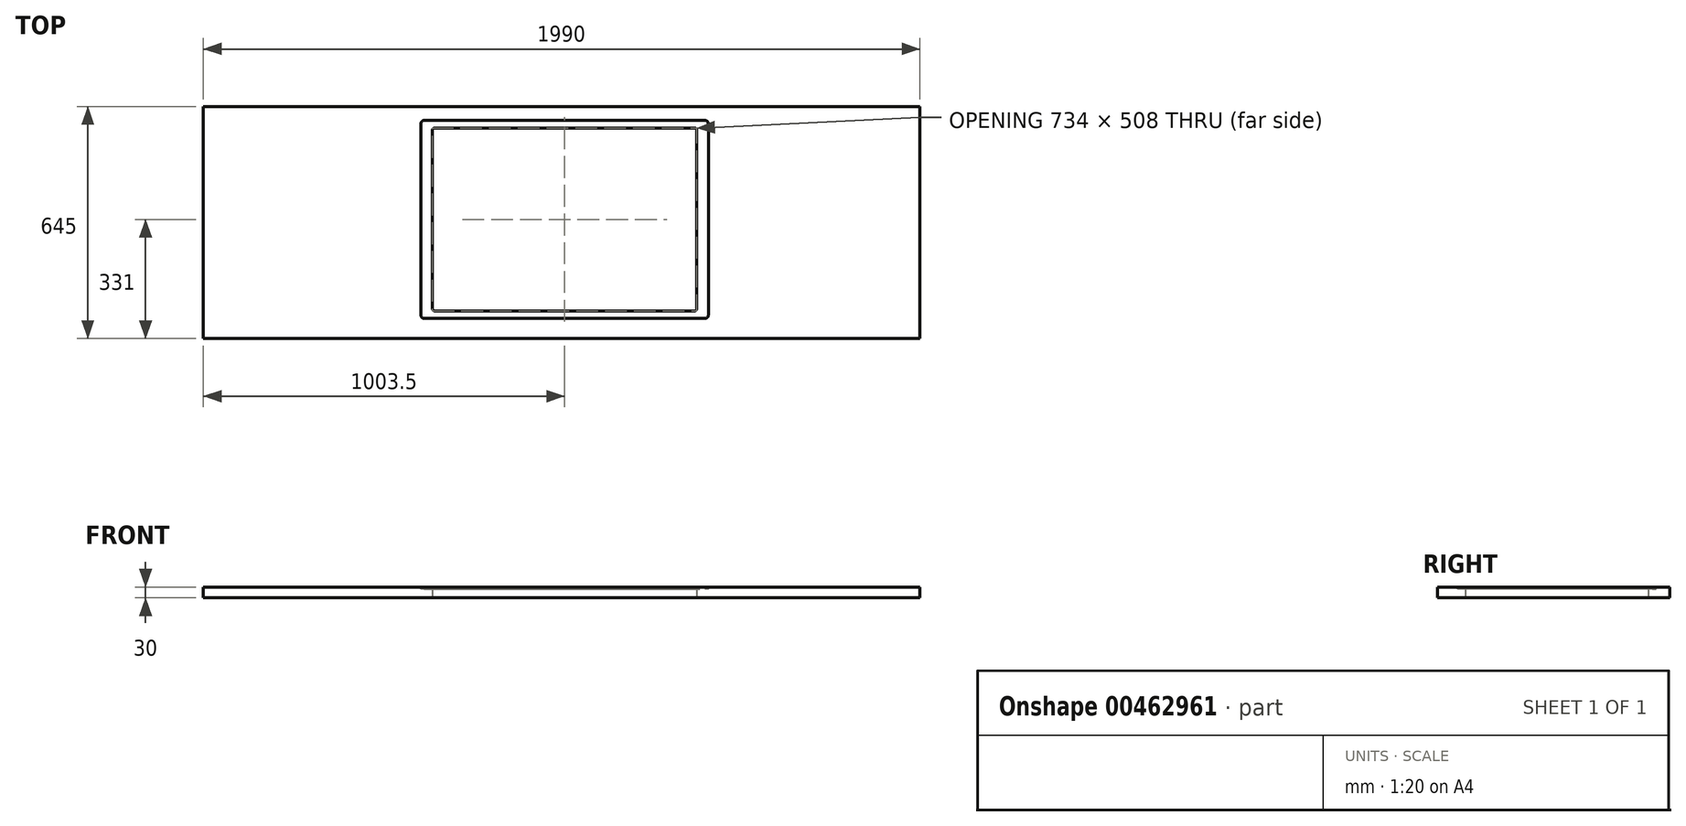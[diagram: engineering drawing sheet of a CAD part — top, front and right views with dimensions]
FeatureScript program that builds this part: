
annotation { "Feature Type Name" : "Feature", "Feature Type Description" : "" }
export const myFeature = defineFeature(function(context is Context, id is Id, definition is map)
    precondition{}
    {
        {
            var Q0;
            Q0=qCreatedBy(makeId("Top.planeOp"),FACE);
            var sketch = newSketch(context, id + "F0", { "sketchPlane" : qUnion([Q0])});
            skLineSegment(sketch, "E0.bottom", {"start": v(0, 0) * mm, "end": v(-1990, 0) * mm});
            skLineSegment(sketch, "E0.top", {"start": v(0, 645) * mm, "end": v(-1990, 645) * mm});
            skLineSegment(sketch, "E0.left", {"start": v(0, 0) * mm, "end": v(0, 645) * mm});
            skLineSegment(sketch, "E0.right", {"start": v(-1990, 0) * mm, "end": v(-1990, 645) * mm});
            skLineSegment(sketch, "E1.bottom", {"start": v(-1347.5, 585) * mm, "end": v(-625.5, 585) * mm});
            skLineSegment(sketch, "E1.top", {"start": v(-1347.5, 77) * mm, "end": v(-625.5, 77) * mm});
            skLineSegment(sketch, "E1.left", {"start": v(-1353.5, 579) * mm, "end": v(-1353.5, 83) * mm});
            skLineSegment(sketch, "E1.right", {"start": v(-619.5, 579) * mm, "end": v(-619.5, 83) * mm});
            skPoint(sketch, "E2.visualSharp", {"position": v(-1353.5, 585) * mm});
            skArc(sketch, "E2.filletArc", {"start": v(-1347.5, 585) * mm, "mid": v(-1351.74, 583.24) * mm, "end": v(-1353.5, 579) * mm});
            skPoint(sketch, "E3.visualSharp", {"position": v(-1353.5, 77) * mm});
            skArc(sketch, "E3.filletArc", {"start": v(-1353.5, 83) * mm, "mid": v(-1351.74, 78.76) * mm, "end": v(-1347.5, 77) * mm});
            skPoint(sketch, "E4.visualSharp", {"position": v(-619.5, 77) * mm});
            skArc(sketch, "E4.filletArc", {"start": v(-625.5, 77) * mm, "mid": v(-621.26, 78.76) * mm, "end": v(-619.5, 83) * mm});
            skPoint(sketch, "E5.visualSharp", {"position": v(-619.5, 585) * mm});
            skArc(sketch, "E5.filletArc", {"start": v(-619.5, 579) * mm, "mid": v(-621.26, 583.24) * mm, "end": v(-625.5, 585) * mm});
            skLineSegment(sketch, "E6", {"start": v(0, 322.5) * mm, "end": v(-1990, 322.5) * mm, "construction": true});
            skSolve(sketch);
        }
        {
            var Q0;
            Q0 = qSketchRegion(id + "F0", true);
            var Q1;
            Q1=makeQuery(id+"F0.imprint","IMPRINT",FACE,{"disambiguationData":[TD([[makeQuery(id+"F0.imprint","IMPRINT",EDGE,{"derivedFrom":sQuery(id+"F0.wireOp",EDGE,"E0.bottom")}),-1.0]])]});
            extrude(context, id + "F1", {"entities" : qUnion([Q0, Q1]), "depth" : 30 * mm});
        }
        {
            var Q0;
            Q0=makeQuery(id+"F1.opExtrude","CAP_FACE",FACE,{"disambiguationData":[OSD([sQuery(id+"F0.wireOp",EDGE,"E0.bottom"),sQuery(id+"F0.wireOp",EDGE,"E0.top"),sQuery(id+"F0.wireOp",EDGE,"E0.left"),sQuery(id+"F0.wireOp",EDGE,"E0.right"),sQuery(id+"F0.wireOp",EDGE,"E1.bottom"),sQuery(id+"F0.wireOp",EDGE,"E1.top"),sQuery(id+"F0.wireOp",EDGE,"E1.left"),sQuery(id+"F0.wireOp",EDGE,"E1.right"),sQuery(id+"F0.wireOp",EDGE,"E2.filletArc"),sQuery(id+"F0.wireOp",EDGE,"E3.filletArc"),sQuery(id+"F0.wireOp",EDGE,"E4.filletArc"),sQuery(id+"F0.wireOp",EDGE,"E5.filletArc")])],"isStart":false});
            var sketch = newSketch(context, id + "F2", { "sketchPlane" : qUnion([Q0])});
            skArc(sketch, "E7.0", {"start": v(-587.5, 597) * mm, "mid": v(-590.14, 603.36) * mm, "end": v(-596.5, 606) * mm});
            skLineSegment(sketch, "E7.1", {"start": v(-1376.5, 606) * mm, "end": v(-596.5, 606) * mm});
            skLineSegment(sketch, "E7.2", {"start": v(-587.5, 597) * mm, "end": v(-587.5, 65) * mm});
            skArc(sketch, "E7.3", {"start": v(-1376.5, 606) * mm, "mid": v(-1382.86, 603.36) * mm, "end": v(-1385.5, 597) * mm});
            skArc(sketch, "E7.4", {"start": v(-596.5, 56) * mm, "mid": v(-590.14, 58.64) * mm, "end": v(-587.5, 65) * mm});
            skLineSegment(sketch, "E7.5", {"start": v(-1376.5, 56) * mm, "end": v(-596.5, 56) * mm});
            skArc(sketch, "E7.6", {"start": v(-1385.5, 65) * mm, "mid": v(-1382.86, 58.64) * mm, "end": v(-1376.5, 56) * mm});
            skLineSegment(sketch, "E7.7", {"start": v(-1385.5, 597) * mm, "end": v(-1385.5, 65) * mm});
            skLineSegment(sketch, "E8", {"start": v(-1353.5, 331) * mm, "end": v(-619.5, 331) * mm, "construction": true});
            skLineSegment(sketch, "E9", {"start": v(-986.5, 585) * mm, "end": v(-986.5, 77) * mm, "construction": true});
            skSolve(sketch);
        }
        {
            var Q0;
            Q0=makeQuery(id+"F2.imprint","IMPRINT",FACE,{"disambiguationData":[TD([[makeQuery(id+"F2.imprint","IMPRINT",EDGE,{"derivedFrom":sQuery(id+"F2.wireOp",EDGE,"E7.0")}),1.0]])]});
            extrude(context, id + "F3", {"entities" : qUnion([Q0]), "operationType" : NewBodyOperationType.REMOVE, "oppositeDirection" : true, "depth" : 5 * mm});
        }
    });
